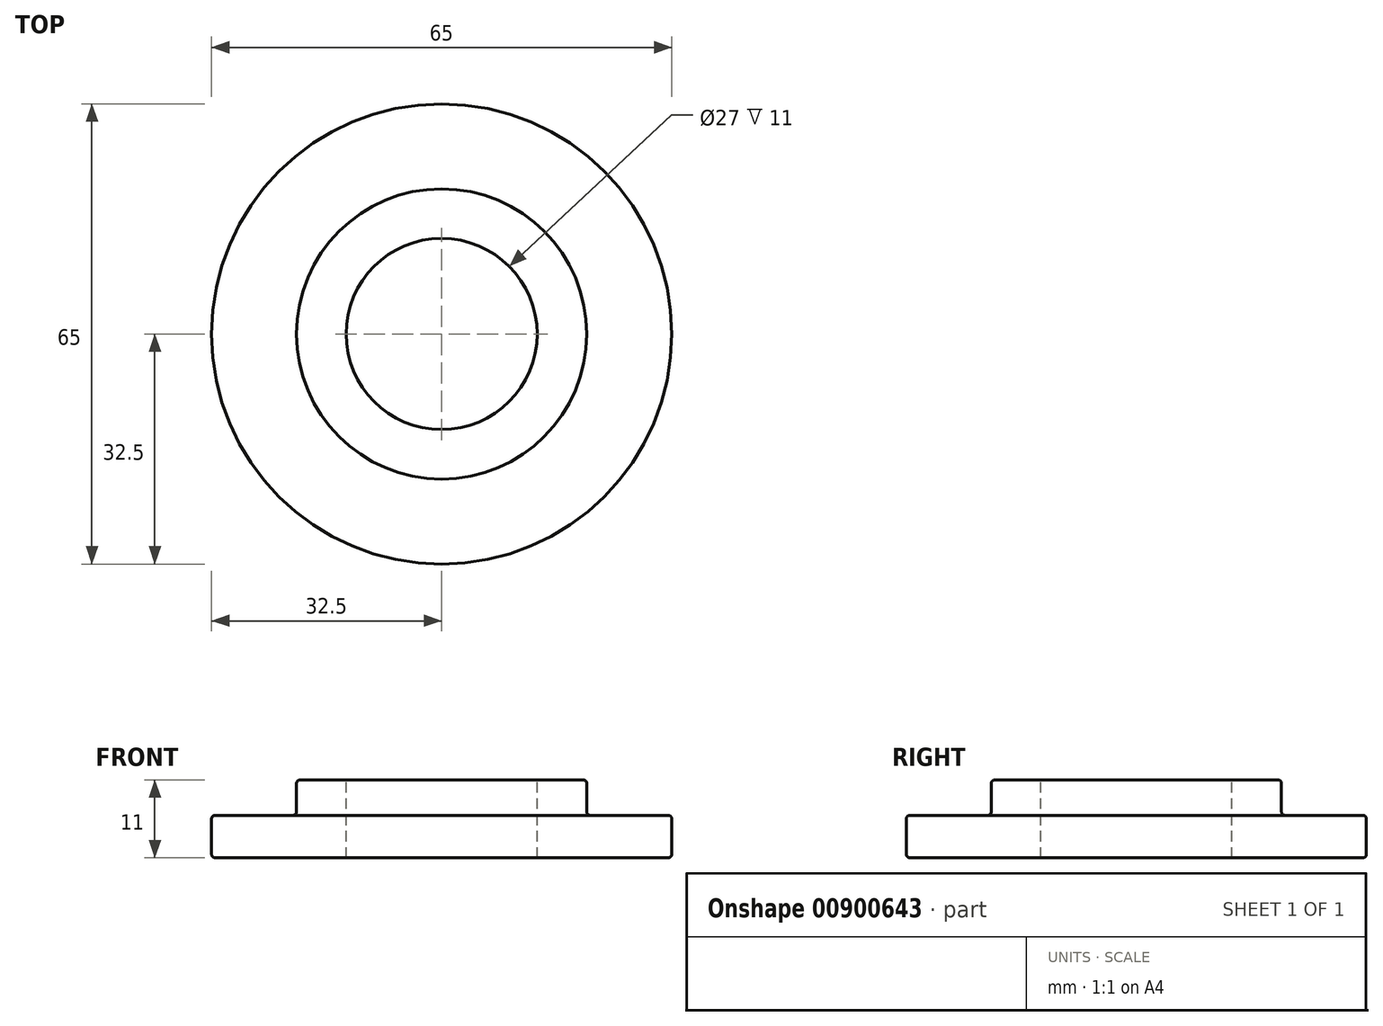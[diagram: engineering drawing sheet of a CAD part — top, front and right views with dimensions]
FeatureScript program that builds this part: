
annotation { "Feature Type Name" : "Feature", "Feature Type Description" : "" }
export const myFeature = defineFeature(function(context is Context, id is Id, definition is map)
    precondition{}
    {
        {
            var Q0;
            Q0=qCreatedBy(makeId("Front.planeOp"),FACE);
            var sketch = newSketch(context, id + "F0", { "sketchPlane" : qUnion([Q0])});
            skLineSegment(sketch, "E0.bottom", {"start": v(13.5, 5.5) * mm, "end": v(20.5, 5.5) * mm});
            skLineSegment(sketch, "E0.top", {"start": v(13.5, -5.5) * mm, "end": v(32.5, -5.5) * mm});
            skLineSegment(sketch, "E0.left", {"start": v(13.5, 5.5) * mm, "end": v(13.5, -5.5) * mm});
            skLineSegment(sketch, "E0.right", {"start": v(32.5, 0.5) * mm, "end": v(32.5, -5.5) * mm});
            skLineSegment(sketch, "E1", {"start": v(0, 10.62) * mm, "end": v(0, -10.98) * mm, "construction": true});
            skLineSegment(sketch, "E2", {"start": v(20.5, 5.5) * mm, "end": v(20.5, 0.5) * mm});
            skLineSegment(sketch, "E3", {"start": v(20.5, 0.5) * mm, "end": v(32.5, 0.5) * mm});
            skSolve(sketch);
        }
        {
            var Q0;
            Q0=makeQuery(id+"F0.imprint","IMPRINT",FACE,{"disambiguationData":[TD([[makeQuery(id+"F0.imprint","IMPRINT",EDGE,{"derivedFrom":sQuery(id+"F0.wireOp",EDGE,"E0.bottom")}),-1.0]])]});
            var Q1;
            Q1=sQuery(id+"F0.wireOp",EDGE,"E1");
            revolve(context, id + "F1", {"surfaceOperationType" : NewSurfaceOperationType.NEW, "entities" : qUnion([Q0]), "axis" : qUnion([Q1]), "revolveType" : RevolveType.FULL});
        }
        {
            var Q0;
            Q0=makeQuery(id+"F1.opRevolve","SWEPT_EDGE",EDGE,{"disambiguationData":[OSD([sQuery(id+"F0.wireOp",EDGE,"E0.top"),sQuery(id+"F0.wireOp",EDGE,"E0.right")])]});
            var Q1;
            Q1=makeQuery(id+"F1.opRevolve","SWEPT_EDGE",EDGE,{"disambiguationData":[OSD([sQuery(id+"F0.wireOp",EDGE,"E0.right"),sQuery(id+"F0.wireOp",EDGE,"E3")])]});
            var Q2;
            Q2=makeQuery(id+"F1.opRevolve","SWEPT_EDGE",EDGE,{"disambiguationData":[OSD([sQuery(id+"F0.wireOp",EDGE,"E0.bottom"),sQuery(id+"F0.wireOp",EDGE,"E2")])]});
            var Q3;
            Q3=makeQuery(id+"F1.opRevolve","SWEPT_EDGE",EDGE,{"disambiguationData":[OSD([sQuery(id+"F0.wireOp",EDGE,"E2"),sQuery(id+"F0.wireOp",EDGE,"E3")])]});
            fillet(context, id + "F2", {"entities" : qUnion([Q0, Q1, Q2, Q3]), "radius" : 0.5 * mm, "tangentPropagation" : true, "allowEdgeOverflow" : false});
        }
    });
